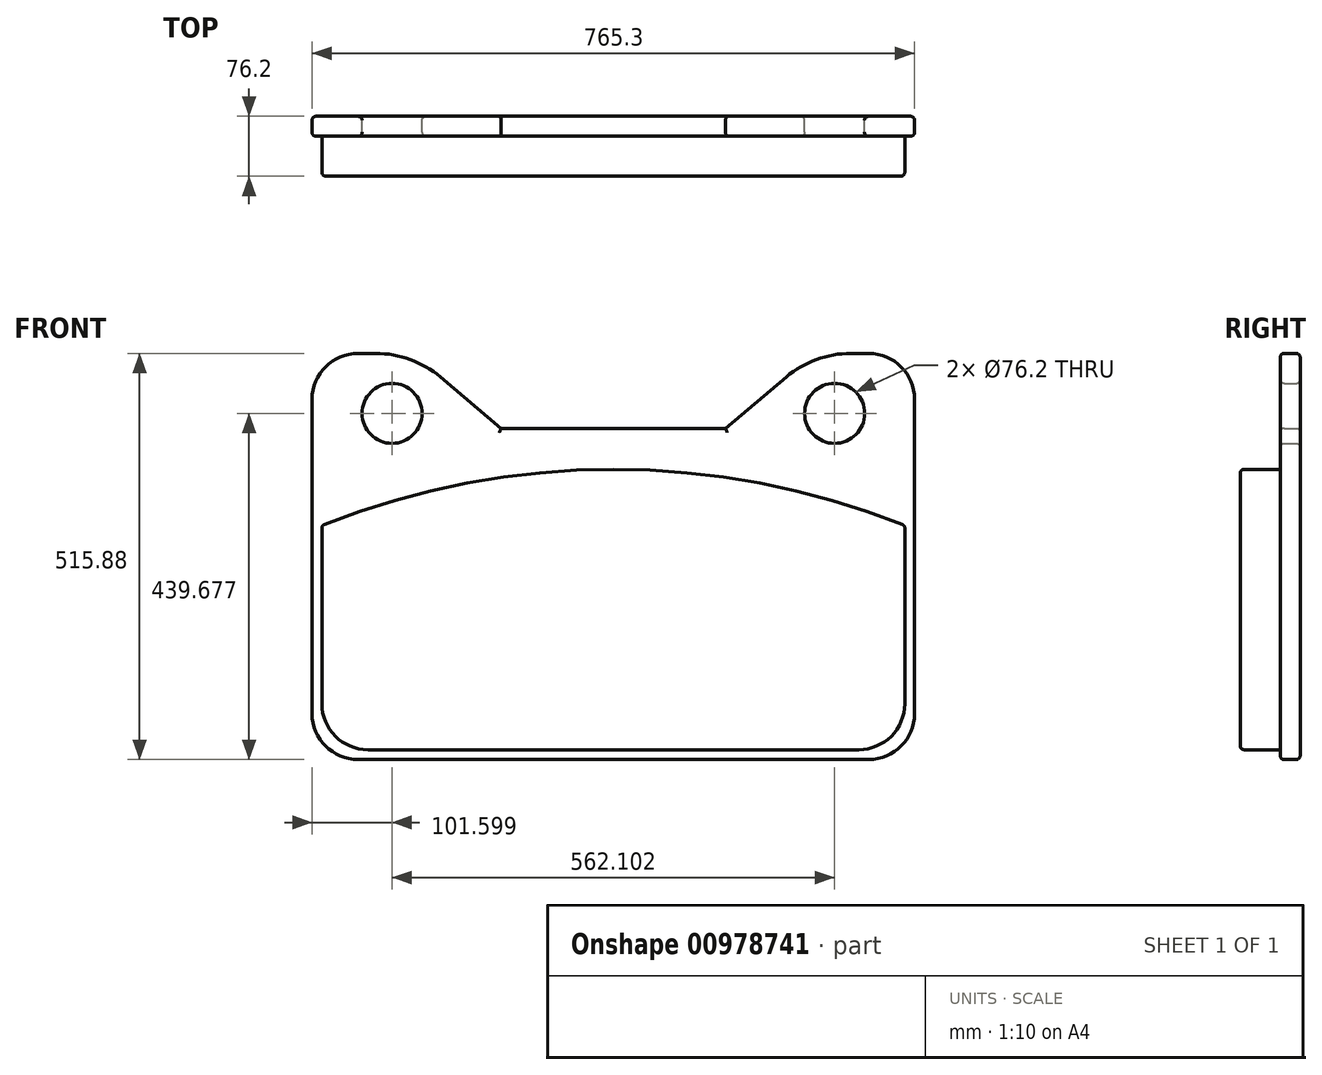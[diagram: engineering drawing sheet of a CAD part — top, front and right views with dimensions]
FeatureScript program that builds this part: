
annotation { "Feature Type Name" : "Feature", "Feature Type Description" : "" }
export const myFeature = defineFeature(function(context is Context, id is Id, definition is map)
    precondition{}
    {
        {
            var Q0;
            Q0=qCreatedBy(makeId("Front.planeOp"),FACE);
            var sketch = newSketch(context, id + "F0", { "sketchPlane" : qUnion([Q0])});
            skLineSegment(sketch, "E0.bottom", {"start": v(324.23, 257.94) * mm, "end": v(301.63, 257.94) * mm});
            skLineSegment(sketch, "E0.top", {"start": v(324.23, -257.94) * mm, "end": v(-324.23, -257.94) * mm});
            skLineSegment(sketch, "E0.left", {"start": v(382.65, 199.52) * mm, "end": v(382.65, -199.52) * mm});
            skLineSegment(sketch, "E0.right", {"start": v(-382.65, 199.52) * mm, "end": v(-382.65, -199.52) * mm});
            skPoint(sketch, "E0.middle", {"position": v(0, 0) * mm});
            skLineSegment(sketch, "E1.bottom", {"start": v(-311.79, -245.5) * mm, "end": v(311.78, -245.5) * mm});
            skLineSegment(sketch, "E1.top", {"start": v(-142.63, 162.85) * mm, "end": v(142.63, 162.85) * mm});
            skLineSegment(sketch, "E1.left", {"start": v(-370.2, -187.07) * mm, "end": v(-370.2, 39.52) * mm});
            skLineSegment(sketch, "E1.right", {"start": v(370.2, -187.07) * mm, "end": v(370.2, 39.52) * mm});
            skLineSegment(sketch, "E2", {"start": v(-219.66, 227.94) * mm, "end": v(-142.63, 162.85) * mm});
            skLineSegment(sketch, "E3", {"start": v(219.66, 227.94) * mm, "end": v(142.63, 162.85) * mm});
            skLineSegment(sketch, "E4.trimOffspring", {"start": v(-301.63, 257.94) * mm, "end": v(-324.23, 257.94) * mm});
            skPoint(sketch, "E5.visualSharp", {"position": v(-382.65, 257.94) * mm});
            skArc(sketch, "E5.filletArc", {"start": v(-324.23, 257.94) * mm, "mid": v(-365.54, 240.83) * mm, "end": v(-382.65, 199.52) * mm});
            skPoint(sketch, "E6.visualSharp", {"position": v(382.65, 257.94) * mm});
            skArc(sketch, "E6.filletArc", {"start": v(382.65, 199.52) * mm, "mid": v(365.54, 240.83) * mm, "end": v(324.23, 257.94) * mm});
            skPoint(sketch, "E7.visualSharp", {"position": v(-370.2, -245.5) * mm});
            skArc(sketch, "E7.filletArc", {"start": v(-370.2, -187.07) * mm, "mid": v(-353.1, -228.38) * mm, "end": v(-311.79, -245.5) * mm});
            skPoint(sketch, "E8.visualSharp", {"position": v(-382.65, -257.94) * mm});
            skArc(sketch, "E8.filletArc", {"start": v(-382.65, -199.52) * mm, "mid": v(-365.54, -240.83) * mm, "end": v(-324.23, -257.94) * mm});
            skPoint(sketch, "E9.visualSharp", {"position": v(370.2, -245.5) * mm});
            skArc(sketch, "E9.filletArc", {"start": v(311.78, -245.5) * mm, "mid": v(353.1, -228.38) * mm, "end": v(370.2, -187.07) * mm});
            skPoint(sketch, "E10.visualSharp", {"position": v(382.65, -257.94) * mm});
            skArc(sketch, "E10.filletArc", {"start": v(324.23, -257.94) * mm, "mid": v(365.54, -240.83) * mm, "end": v(382.65, -199.52) * mm});
            skPoint(sketch, "E11.visualSharp", {"position": v(-255.16, 257.94) * mm});
            skArc(sketch, "E11.filletArc", {"start": v(-219.66, 227.94) * mm, "mid": v(-257.99, 250.2) * mm, "end": v(-301.63, 257.94) * mm});
            skPoint(sketch, "E12.visualSharp", {"position": v(255.16, 257.94) * mm});
            skArc(sketch, "E12.filletArc", {"start": v(301.63, 257.94) * mm, "mid": v(257.99, 250.2) * mm, "end": v(219.66, 227.94) * mm});
            skArc(sketch, "E13", {"start": v(370.2, 39.52) * mm, "mid": v(0, 110.68) * mm, "end": v(-370.2, 39.52) * mm});
            skCircle(sketch, "E14", {"center": v(-281.05, 181.74) * mm, "radius": 38.1 * mm});
            skCircle(sketch, "E15", {"center": v(281.05, 181.74) * mm, "radius": 38.1 * mm});
            skSolve(sketch);
        }
        {
            var Q0;
            Q0=makeQuery(id+"F0.imprint","IMPRINT",FACE,{"disambiguationData":[TD([[makeQuery(id+"F0.imprint","IMPRINT",EDGE,{"derivedFrom":sQuery(id+"F0.wireOp",EDGE,"E1.bottom")}),1.0]])]});
            extrude(context, id + "F1", {"entities" : qUnion([Q0]), "depth" : 76.2 * mm, "offsetDistance" : 25.4 * mm});
        }
        {
            var Q0;
            Q0=makeQuery(id+"F0.imprint","IMPRINT",FACE,{"disambiguationData":[TD([[makeQuery(id+"F0.imprint","IMPRINT",EDGE,{"derivedFrom":sQuery(id+"F0.wireOp",EDGE,"E0.bottom")}),1.0]])]});
            extrude(context, id + "F2", {"entities" : qUnion([Q0]), "operationType" : NewBodyOperationType.ADD, "depth" : 25.4 * mm, "offsetDistance" : 25.4 * mm});
        }
        {
            var Q0;
            Q0=makeQuery(id+"F2.opExtrude","CAP_EDGE",EDGE,{"disambiguationData":[OSD([sQuery(id+"F0.wireOp",EDGE,"E0.right")])],"isStart":false});
            var Q1;
            Q1=makeQuery(id+"F2.opExtrude","CAP_EDGE",EDGE,{"disambiguationData":[OSD([sQuery(id+"F0.wireOp",EDGE,"E5.filletArc")])],"isStart":false});
            var Q2;
            Q2=makeQuery(id+"F2.opExtrude","CAP_EDGE",EDGE,{"disambiguationData":[OSD([sQuery(id+"F0.wireOp",EDGE,"E4.trimOffspring")])],"isStart":false});
            var Q3;
            Q3=makeQuery(id+"F2.opExtrude","CAP_EDGE",EDGE,{"disambiguationData":[OSD([sQuery(id+"F0.wireOp",EDGE,"E11.filletArc")])],"isStart":false});
            var Q4;
            Q4=makeQuery(id+"F2.opExtrude","CAP_EDGE",EDGE,{"disambiguationData":[OSD([sQuery(id+"F0.wireOp",EDGE,"E2")])],"isStart":false});
            var Q5;
            Q5=makeQuery(id+"F2.opExtrude","CAP_EDGE",EDGE,{"disambiguationData":[OSD([sQuery(id+"F0.wireOp",EDGE,"E1.top")])],"isStart":false});
            var Q6;
            Q6=makeQuery(id+"F2.opExtrude","CAP_EDGE",EDGE,{"disambiguationData":[OSD([sQuery(id+"F0.wireOp",EDGE,"E3")])],"isStart":false});
            var Q7;
            Q7=makeQuery(id+"F2.opExtrude","CAP_EDGE",EDGE,{"disambiguationData":[OSD([sQuery(id+"F0.wireOp",EDGE,"E12.filletArc")])],"isStart":false});
            var Q8;
            Q8=makeQuery(id+"F2.opExtrude","CAP_EDGE",EDGE,{"disambiguationData":[OSD([sQuery(id+"F0.wireOp",EDGE,"E0.bottom")])],"isStart":false});
            var Q9;
            Q9=makeQuery(id+"F2.opExtrude","CAP_EDGE",EDGE,{"disambiguationData":[OSD([sQuery(id+"F0.wireOp",EDGE,"E6.filletArc")])],"isStart":false});
            var Q10;
            Q10=makeQuery(id+"F2.opExtrude","CAP_EDGE",EDGE,{"disambiguationData":[OSD([sQuery(id+"F0.wireOp",EDGE,"E0.left")])],"isStart":false});
            var Q11;
            Q11=makeQuery(id+"F2.opExtrude","CAP_EDGE",EDGE,{"disambiguationData":[OSD([sQuery(id+"F0.wireOp",EDGE,"E10.filletArc")])],"isStart":false});
            var Q12;
            Q12=makeQuery(id+"F2.opExtrude","CAP_EDGE",EDGE,{"disambiguationData":[OSD([sQuery(id+"F0.wireOp",EDGE,"E0.top")])],"isStart":false});
            var Q13;
            Q13=makeQuery(id+"F1.opExtrude","CAP_EDGE",EDGE,{"disambiguationData":[OSD([sQuery(id+"F0.wireOp",EDGE,"E9.filletArc")])],"isStart":false});
            var Q14;
            Q14=makeQuery(id+"F1.opExtrude","CAP_EDGE",EDGE,{"disambiguationData":[OSD([sQuery(id+"F0.wireOp",EDGE,"E1.right")])],"isStart":false});
            var Q15;
            Q15=makeQuery(id+"F1.opExtrude","CAP_EDGE",EDGE,{"disambiguationData":[OSD([sQuery(id+"F0.wireOp",EDGE,"E1.bottom")])],"isStart":false});
            var Q16;
            Q16=makeQuery(id+"F1.opExtrude","CAP_EDGE",EDGE,{"disambiguationData":[OSD([sQuery(id+"F0.wireOp",EDGE,"E13")])],"isStart":false});
            var Q17;
            Q17=makeQuery(id+"F2.opExtrude","CAP_EDGE",EDGE,{"disambiguationData":[OSD([sQuery(id+"F0.wireOp",EDGE,"E0.right")])],"isStart":true});
            var Q18;
            Q18=makeQuery(id+"F2.opExtrude","CAP_EDGE",EDGE,{"disambiguationData":[OSD([sQuery(id+"F0.wireOp",EDGE,"E5.filletArc")])],"isStart":true});
            var Q19;
            Q19=makeQuery(id+"F2.opExtrude","CAP_EDGE",EDGE,{"disambiguationData":[OSD([sQuery(id+"F0.wireOp",EDGE,"E0.left")])],"isStart":true});
            var Q20;
            Q20=makeQuery(id+"F2.opExtrude","CAP_EDGE",EDGE,{"disambiguationData":[OSD([sQuery(id+"F0.wireOp",EDGE,"E6.filletArc")])],"isStart":true});
            var Q21;
            Q21=makeQuery(id+"F2.opExtrude","CAP_EDGE",EDGE,{"disambiguationData":[OSD([sQuery(id+"F0.wireOp",EDGE,"E0.bottom")])],"isStart":true});
            var Q22;
            Q22=makeQuery(id+"F2.opExtrude","CAP_EDGE",EDGE,{"disambiguationData":[OSD([sQuery(id+"F0.wireOp",EDGE,"E1.top")])],"isStart":true});
            var Q23;
            Q23=makeQuery(id+"F2.opExtrude","CAP_EDGE",EDGE,{"disambiguationData":[OSD([sQuery(id+"F0.wireOp",EDGE,"E2")])],"isStart":true});
            var Q24;
            Q24=makeQuery(id+"F2.opExtrude","CAP_EDGE",EDGE,{"disambiguationData":[OSD([sQuery(id+"F0.wireOp",EDGE,"E15")])],"isStart":true});
            var Q25;
            Q25=makeQuery(id+"F2.opExtrude","CAP_EDGE",EDGE,{"disambiguationData":[OSD([sQuery(id+"F0.wireOp",EDGE,"E15")])],"isStart":false});
            var Q26;
            Q26=makeQuery(id+"F1.opExtrude","SWEPT_EDGE",EDGE,{"disambiguationData":[OSD([sQuery(id+"F0.wireOp",EDGE,"E1.right"),sQuery(id+"F0.wireOp",EDGE,"E13")])]});
            var Q27;
            Q27=makeQuery(id+"F1.opExtrude","CAP_EDGE",EDGE,{"disambiguationData":[OSD([sQuery(id+"F0.wireOp",EDGE,"E1.left")])],"isStart":false});
            var Q28;
            Q28=makeQuery(id+"F1.opExtrude","SWEPT_EDGE",EDGE,{"disambiguationData":[OSD([sQuery(id+"F0.wireOp",EDGE,"E1.left"),sQuery(id+"F0.wireOp",EDGE,"E13")])]});
            var Q29;
            Q29=makeQuery(id+"F1.opExtrude","CAP_EDGE",EDGE,{"disambiguationData":[OSD([sQuery(id+"F0.wireOp",EDGE,"E7.filletArc")])],"isStart":false});
            var Q30;
            Q30=makeQuery(id+"F2.opExtrude","CAP_EDGE",EDGE,{"disambiguationData":[OSD([sQuery(id+"F0.wireOp",EDGE,"E8.filletArc")])],"isStart":false});
            var Q31;
            Q31=makeQuery(id+"F2.opExtrude","CAP_EDGE",EDGE,{"disambiguationData":[OSD([sQuery(id+"F0.wireOp",EDGE,"E8.filletArc")])],"isStart":true});
            var Q32;
            Q32=makeQuery(id+"F2.opExtrude","CAP_EDGE",EDGE,{"disambiguationData":[OSD([sQuery(id+"F0.wireOp",EDGE,"E14")])],"isStart":false});
            var Q33;
            Q33=makeQuery(id+"F2.opExtrude","CAP_EDGE",EDGE,{"disambiguationData":[OSD([sQuery(id+"F0.wireOp",EDGE,"E14")])],"isStart":true});
            var Q34;
            Q34=makeQuery(id+"F2.opExtrude","CAP_EDGE",EDGE,{"disambiguationData":[OSD([sQuery(id+"F0.wireOp",EDGE,"E4.trimOffspring")])],"isStart":true});
            var Q35;
            Q35=makeQuery(id+"F2.opExtrude","CAP_EDGE",EDGE,{"disambiguationData":[OSD([sQuery(id+"F0.wireOp",EDGE,"E11.filletArc")])],"isStart":true});
            var Q36;
            Q36=makeQuery(id+"F2.opExtrude","CAP_EDGE",EDGE,{"disambiguationData":[OSD([sQuery(id+"F0.wireOp",EDGE,"E12.filletArc")])],"isStart":true});
            var Q37;
            Q37=makeQuery(id+"F2.opExtrude","CAP_EDGE",EDGE,{"disambiguationData":[OSD([sQuery(id+"F0.wireOp",EDGE,"E3")])],"isStart":true});
            var Q38;
            Q38=makeQuery(id+"F2.opExtrude","CAP_EDGE",EDGE,{"disambiguationData":[OSD([sQuery(id+"F0.wireOp",EDGE,"E10.filletArc")])],"isStart":true});
            fillet(context, id + "F3", {"entities" : qUnion([Q0, Q1, Q2, Q3, Q4, Q5, Q6, Q7, Q8, Q9, Q10, Q11, Q12, Q13, Q14, Q15, Q16, Q17, Q18, Q19, Q20, Q21, Q22, Q23, Q24, Q25, Q26, Q27, Q28, Q29, Q30, Q31, Q32, Q33, Q34, Q35, Q36, Q37, Q38]), "radius" : 5.08 * mm, "tangentPropagation" : true, "allowEdgeOverflow" : false});
        }
    });
